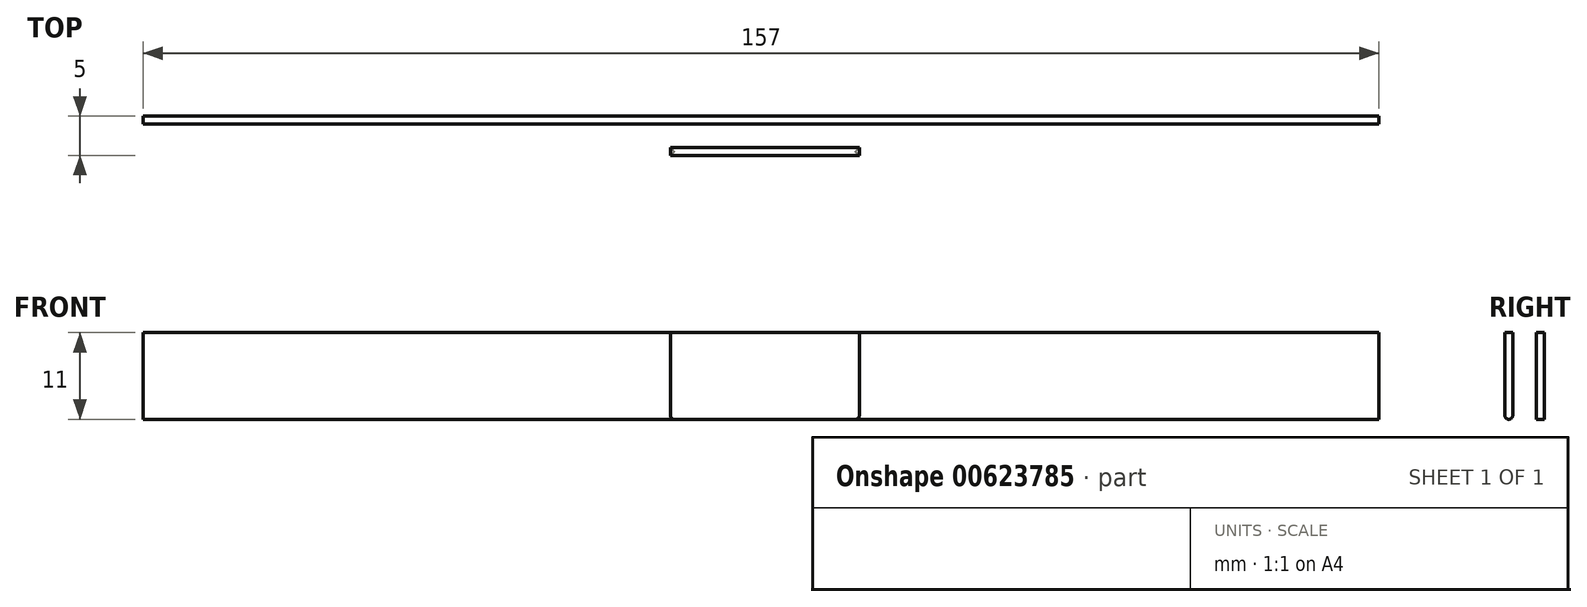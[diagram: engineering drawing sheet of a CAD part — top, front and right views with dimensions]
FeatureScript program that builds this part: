
annotation { "Feature Type Name" : "Feature", "Feature Type Description" : "" }
export const myFeature = defineFeature(function(context is Context, id is Id, definition is map)
    precondition{}
    {
        {
            var Q0;
            Q0=qCreatedBy(makeId("Top.planeOp"),FACE);
            var sketch = newSketch(context, id + "F0", { "sketchPlane" : qUnion([Q0])});
            skLineSegment(sketch, "E0.bottom", {"start": v(-62, 0) * mm, "end": v(95, 0) * mm});
            skLineSegment(sketch, "E0.top", {"start": v(-62, -4) * mm, "end": v(95, -4) * mm});
            skLineSegment(sketch, "E0.left", {"start": v(-62, 0) * mm, "end": v(-62, -4) * mm});
            skLineSegment(sketch, "E0.right", {"start": v(95, 0) * mm, "end": v(95, -4) * mm});
            skLineSegment(sketch, "E1", {"start": v(0, 0) * mm, "end": v(0, 0) * mm});
            skLineSegment(sketch, "E2", {"start": v(0, 0) * mm, "end": v(95, 0) * mm, "construction": true});
            skLineSegment(sketch, "E3.left", {"start": v(-62, 0) * mm, "end": v(-62, 0) * mm});
            skLineSegment(sketch, "E3.right", {"start": v(95, 0) * mm, "end": v(95, 0) * mm});
            skLineSegment(sketch, "E4.top", {"start": v(-62, -1) * mm, "end": v(95, -1) * mm});
            skLineSegment(sketch, "E4.left", {"start": v(-62, 0) * mm, "end": v(-62, -1) * mm});
            skLineSegment(sketch, "E4.right", {"start": v(95, 0) * mm, "end": v(95, -1) * mm});
            skLineSegment(sketch, "E5.top", {"start": v(-62, -3) * mm, "end": v(95, -3) * mm});
            skLineSegment(sketch, "E5.left", {"start": v(-62, -4) * mm, "end": v(-62, -3) * mm});
            skLineSegment(sketch, "E5.right", {"start": v(95, -4) * mm, "end": v(95, -3) * mm});
            skLineSegment(sketch, "E6.bottom", {"start": v(5, -4) * mm, "end": v(29, -4) * mm});
            skLineSegment(sketch, "E6.top", {"start": v(5, -5) * mm, "end": v(29, -5) * mm});
            skLineSegment(sketch, "E6.left", {"start": v(5, -4) * mm, "end": v(5, -5) * mm});
            skLineSegment(sketch, "E6.right", {"start": v(29, -4) * mm, "end": v(29, -5) * mm});
            skLineSegment(sketch, "E7", {"start": v(-62, -4) * mm, "end": v(5, -4) * mm, "construction": true});
            skLineSegment(sketch, "E8.bottom", {"start": v(6, -4) * mm, "end": v(28, -4) * mm});
            skLineSegment(sketch, "E8.top", {"start": v(6, -3) * mm, "end": v(28, -3) * mm});
            skLineSegment(sketch, "E8.left", {"start": v(6, -4) * mm, "end": v(6, -3) * mm});
            skLineSegment(sketch, "E8.right", {"start": v(28, -4) * mm, "end": v(28, -3) * mm});
            skLineSegment(sketch, "E9", {"start": v(5, -4) * mm, "end": v(6, -4) * mm, "construction": true});
            skSolve(sketch);
        }
        {
            var Q0;
            {var subQ1=sQuery(id+"F0.wireOp",EDGE,"E0.left");Q0=makeQuery(id+"F0.imprint","IMPRINT",FACE,{"disambiguationData":[TD([[makeQuery(id+"F0.imprint","IMPRINT",EDGE,{"derivedFrom":subQ1}),1.0]])]});}
            var Q1;
            Q1=makeQuery(id+"F0.imprint","IMPRINT",FACE,{"disambiguationData":[TD([[makeQuery(id+"F0.imprint","IMPRINT",EDGE,{"derivedFrom":sQuery(id+"F0.wireOp",EDGE,"E8.bottom")}),1.0]])]});
            extrude(context, id + "F1", {"entities" : qUnion([Q0, Q1]), "depth" : 1 * mm, "offsetDistance" : 25 * mm});
        }
        {
            var Q0;
            Q0=makeQuery(id+"F0.imprint","IMPRINT",FACE,{"disambiguationData":[TD([[makeQuery(id+"F0.imprint","IMPRINT",EDGE,{"derivedFrom":sQuery(id+"F0.wireOp",EDGE,"E6.top")}),1.0]])]});
            var Q1;
            {var subQ4=sQuery(id+"F0.wireOp",EDGE,"E5.left");Q1=makeQuery(id+"F0.imprint","IMPRINT",FACE,{"disambiguationData":[TD([[makeQuery(id+"F0.imprint","IMPRINT",EDGE,{"derivedFrom":subQ4}),-1.0]])]});}
            var Q2;
            {var subQ4=sQuery(id+"F0.wireOp",EDGE,"E5.right");Q2=makeQuery(id+"F0.imprint","IMPRINT",FACE,{"disambiguationData":[TD([[makeQuery(id+"F0.imprint","IMPRINT",EDGE,{"derivedFrom":subQ4}),1.0]])]});}
            var Q3;
            Q3=makeQuery(id+"F0.imprint","IMPRINT",FACE,{"disambiguationData":[TD([[makeQuery(id+"F0.imprint","IMPRINT",EDGE,{"derivedFrom":sQuery(id+"F0.wireOp",EDGE,"E0.bottom")}),-1.0]])]});
            extrude(context, id + "F2", {"entities" : qUnion([Q0, Q1, Q2, Q3]), "operationType" : NewBodyOperationType.ADD, "depth" : 11 * mm, "offsetDistance" : 25 * mm});
        }
        {
            var Q0;
            Q0=makeQuery(id+"F2.opExtrude","CAP_EDGE",EDGE,{"disambiguationData":[OSD([sQuery(id+"F0.wireOp",EDGE,"E6.top")])],"isStart":true});
            var Q1;
            Q1=makeQuery(id+"F2.opExtrude","CAP_EDGE",EDGE,{"disambiguationData":[OSD([sQuery(id+"F0.wireOp",EDGE,"E6.left")])],"isStart":true});
            var Q2;
            {var subQ0=sQuery(id+"F0.wireOp",EDGE,"E0.top");Q2=makeQuery(id+"F2.opExtrude","CAP_EDGE",EDGE,{"disambiguationData":[OSD([subQ0]),TDD([makeQuery(id+"F0.imprint","IMPRINT",EDGE,{"disambiguationData":[TD([[makeQuery(id+"F0.imprint","INTERSECT",VERTEX,{"derivedFrom":[subQ0,sQuery(id+"F0.wireOp",EDGE,"E5.left")]}),-1.0]])],"derivedFrom":subQ0})])],"isStart":true});}
            var Q3;
            {var subQ0=sQuery(id+"F0.wireOp",EDGE,"E0.top");Q3=makeQuery(id+"F2.opExtrude","CAP_EDGE",EDGE,{"disambiguationData":[OSD([subQ0]),TDD([makeQuery(id+"F0.imprint","IMPRINT",EDGE,{"disambiguationData":[TD([[makeQuery(id+"F0.imprint","INTERSECT",VERTEX,{"derivedFrom":[subQ0,sQuery(id+"F0.wireOp",EDGE,"E5.right")]}),1.0]])],"derivedFrom":subQ0})])],"isStart":true});}
            var Q4;
            Q4=makeQuery(id+"F2.opExtrude","CAP_EDGE",EDGE,{"disambiguationData":[OSD([sQuery(id+"F0.wireOp",EDGE,"E6.right")])],"isStart":true});
            var Q5;
            Q5=makeQuery(id+"F2.opExtrude","CAP_EDGE",EDGE,{"disambiguationData":[OSD([sQuery(id+"F0.wireOp",EDGE,"E0.bottom")])],"isStart":true});
            fillet(context, id + "F3", {"entities" : qUnion([Q0, Q1, Q2, Q3, Q4, Q5]), "radius" : .5 * mm, "tangentPropagation" : true, "allowEdgeOverflow" : false});
        }
    });
